# Revit family: Scale-SR_Scales-SR7001i
name_source: partatom
category: Specialty Equipment
units: mm (PartAtom-declared; Revit-internal decimal feet)

## family parameters
Always vertical = Yes
Cut with Voids When Loaded = No
Maintain Annotation Orientation = No
OmniClass Number = 23.40.70.11.14.11
OmniClass Title = Medical Equipment
Part Type = Normal
Room Calculation Point = No
Round Connector Dimension = Use Diameter
Shared = No
Work Plane-Based = No

## types (2) — shared parameters
Accuracy = 0.1% +/- 1 Digit of Displayed Resolution
Assembly Code = E1020810
Auto Power Down = 30 to 300 Seconds
Auto Zero = Fold Unit Down or Press Button
Averaging = Automatic Digital Filter
BIM Version = v4.2
BIM Version Available (Earliest) = 2022
Calibration = Traceable to NIST Standards
Default Elevation = 0"
Display Resolution = 0.1 lb / 0.1 kg
Display Type = 16-Character LCD with LED Backlight
Display Units = Pounds / Kilograms
Housing Depth = 3 1/4"
Housing Height = 38"
Housing Width = 48"
Manufacturer = SR Scales by SR Instruments, Inc.
Maximum Weight Capacity = 600 lbs or 300 kg
Memory Recall = Recalls Last Stored Weight
Platform Depth = 30"
Platform Size = 24'' x 30'' (61 cm x 76.2 cm)
Platform Width = 24"
Power Supply = AC Wall Power Supply, UL Recognized
Product Page URL = https://srinstruments.com
Projection From Wall Folded Down = 34"
URL = http://www.srinstruments.com

## per-type parameters (varying)
| type | Description | Show Printer |
| SR7001i | 24" x 30" Wall Mount Platform Scale | No |
| SR7001i-P | 24" x 30" Wall Mount Platform Scale with Printer | Yes |

note: column(s) folded — value = type name in every type: Model

## geometry (parser evidence)
native form markers: Sweep x5
no freeform markers — native parametric forms only
